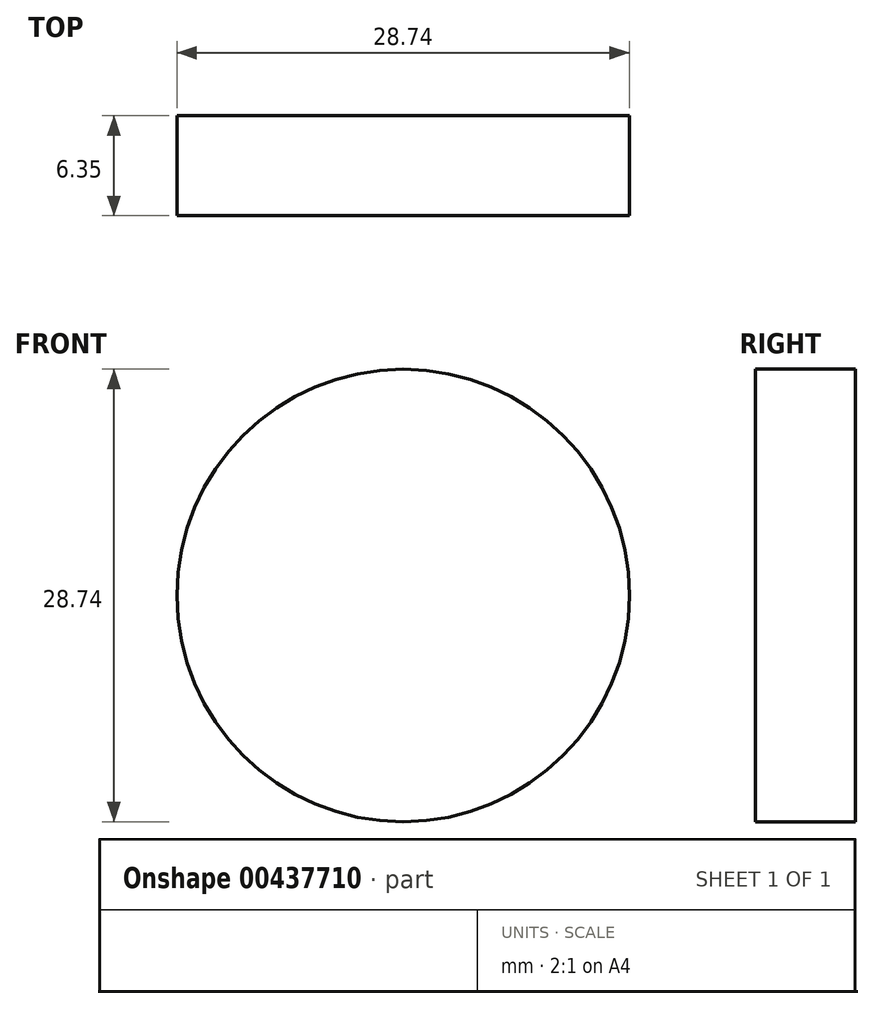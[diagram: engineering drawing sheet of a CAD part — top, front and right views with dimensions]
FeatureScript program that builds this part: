
annotation { "Feature Type Name" : "Feature", "Feature Type Description" : "" }
export const myFeature = defineFeature(function(context is Context, id is Id, definition is map)
    precondition{}
    {
        {
            var Q0;
            Q0=qCreatedBy(makeId("Front.planeOp"),FACE);
            var sketch = newSketch(context, id + "F0", { "sketchPlane" : qUnion([Q0])});
            skCircle(sketch, "E0", {"center": v(0, 0) * mm, "radius": 14.37 * mm});
            skSolve(sketch);
        }
        {
            var Q0;
            Q0=makeQuery(id+"F0.imprint","IMPRINT",FACE,{"disambiguationData":[TD([[makeQuery(id+"F0.imprint","IMPRINT",EDGE,{"derivedFrom":sQuery(id+"F0.wireOp",EDGE,"E0")}),1.0]])]});
            extrude(context, id + "F1", {"entities" : qUnion([Q0]), "depth" : 6.35 * mm});
        }
    });
